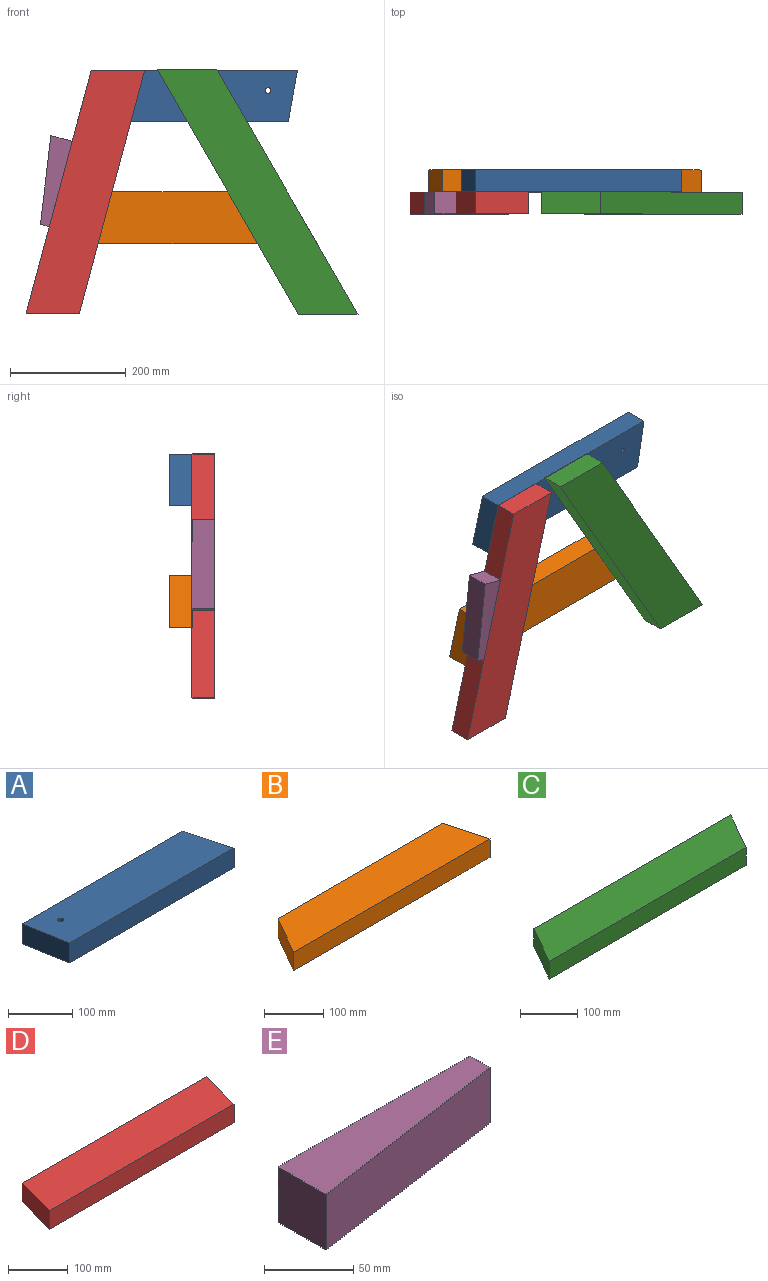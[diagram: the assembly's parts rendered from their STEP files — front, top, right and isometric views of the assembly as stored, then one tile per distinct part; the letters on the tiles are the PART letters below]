
ASSEMBLY  parts=5 mates=4
PART A: 7 faces, bbox 379.4x88.9x38.1 mm
  f0: plane 355.59x38.1mm, normal (0,1,0), area 13548mm2, adj f1,f4,f5,f6
  f1: plane 88.9x38.1mm, normal (-0.98,-0.17,0), area 3439.3mm2, adj f0,f2,f5,f6
  f2: plane 363.74x38.1mm, normal (0,-1,0), area 13858.4mm2, adj f1,f4,f5,f6
  f3: cylinder r=4.76mm len=38.1mm, axis (0,0,-1), area 1140.1mm2, adj f5,f6
  f4: plane 88.9x38.1mm, normal (0.97,0.26,0), area 3506.6mm2, adj f0,f2,f5,f6
  f5: plane 379.41x88.9mm, normal (0,0,1), area 31902.9mm2, adj f0,f1,f2,f3,f4
  f6: plane 379.41x88.9mm, normal (0,0,-1), area 31902.9mm2, adj f0,f1,f2,f3,f4
PART B: 6 faces, bbox 469.9x88.9x38.1 mm
  f0: plane 88.9x38.1mm, normal (0.97,0.26,0), area 3506.6mm2, adj f1,f3,f4,f5
  f1: plane 394.75x38.1mm, normal (0,1,0), area 15040.1mm2, adj f0,f2,f4,f5
  f2: plane 88.9x51.33mm, normal (-0.87,0.5,0), area 3911.1mm2, adj f1,f3,f4,f5
  f3: plane 469.9x38.1mm, normal (0,-1,0), area 17903.2mm2, adj f0,f2,f4,f5
  f4: plane 469.9x88.9mm, normal (0,0,1), area 38433.8mm2, adj f0,f1,f2,f3
  f5: plane 469.9x88.9mm, normal (0,0,-1), area 38433.8mm2, adj f0,f1,f2,f3
PART C: 6 faces, bbox 538.2x88.9x38.1 mm
  f0: plane 486.84x38.1mm, normal (0,1,0), area 18548.5mm2, adj f1,f3,f4,f5
  f1: plane 88.9x51.33mm, normal (-0.87,0.5,0), area 3911.1mm2, adj f0,f2,f4,f5
  f2: plane 486.84x38.1mm, normal (0,-1,0), area 18548.5mm2, adj f1,f3,f4,f5
  f3: plane 88.9x51.33mm, normal (0.87,-0.5,0), area 3911.1mm2, adj f0,f2,f4,f5
  f4: plane 538.16x88.9mm, normal (0,0,1), area 43279.7mm2, adj f0,f1,f2,f3
  f5: plane 538.16x88.9mm, normal (0,0,-1), area 43279.7mm2, adj f0,f1,f2,f3
PART D: 6 faces, bbox 458.8x88.9x38.1 mm
  f0: plane 434.97x38.1mm, normal (0,1,0), area 16572.2mm2, adj f1,f3,f4,f5
  f1: plane 88.9x38.1mm, normal (-0.97,0.26,0), area 3506.6mm2, adj f0,f2,f4,f5
  f2: plane 434.97x38.1mm, normal (0,-1,0), area 16572.2mm2, adj f1,f3,f4,f5
  f3: plane 88.9x38.1mm, normal (0.97,-0.26,0), area 3506.6mm2, adj f0,f2,f4,f5
  f4: plane 458.79x88.9mm, normal (0,0,1), area 38668.5mm2, adj f0,f1,f2,f3
  f5: plane 458.79x88.9mm, normal (0,0,-1), area 38668.5mm2, adj f0,f1,f2,f3
PART E: 6 faces, bbox 152.4x38.1x38.1 mm
  f0: plane 152.4x38.1mm, normal (0,1,0), area 5806.4mm2, adj f1,f3,f4,f5
  f1: plane 38.1x38.1mm, normal (-1,0,0), area 1451.6mm2, adj f0,f2,f4,f5
  f2: plane 152.4x38.1mm, normal (0.14,-0.99,0), area 5867.9mm2, adj f1,f3,f4,f5
  f3: plane 38.1x15.88mm, normal (1,0,0), area 604.8mm2, adj f0,f2,f4,f5
  f4: plane 152.4x38.1mm, normal (0,0,1), area 4112.9mm2, adj f0,f1,f2,f3
  f5: plane 152.4x38.1mm, normal (0,0,-1), area 4112.9mm2, adj f0,f1,f2,f3
PLACE A rot(axis=(0,-0.71,-0.71),180deg) t=(-238.89,19.05,376.43)mm
PLACE B rot(axis=(0,-0.71,-0.71),180deg) t=(-279.67,19.05,166.36)mm
PLACE C rot(axis=(0.77,0.45,-0.45),104.5deg) t=(-121.71,19.05,210.81)mm fixed
PLACE D rot(axis=(-0.68,-0.52,-0.52),111.8deg) t=(-419.12,-19.05,210.81)mm
PLACE E rot(axis=(0.48,0.62,-0.62),129deg) t=(-461.44,19.05,224.6)mm
MATE fastened D.f2 <-> E.f0  axis (-0.97,0,0.26) through (-408.85,19.05,420.88)mm
MATE fastened D.f2 <-> A.f4  axis (-0.97,0,0.26) through (-408.85,19.05,420.88)mm
MATE fastened B.f2 <-> C.f0  axis (0.87,0,0.5) through (-70.38,19.05,210.81)mm
MATE fastened B.f0 <-> D.f2  axis (-0.97,0,0.26) through (-465.14,19.05,210.81)mm
